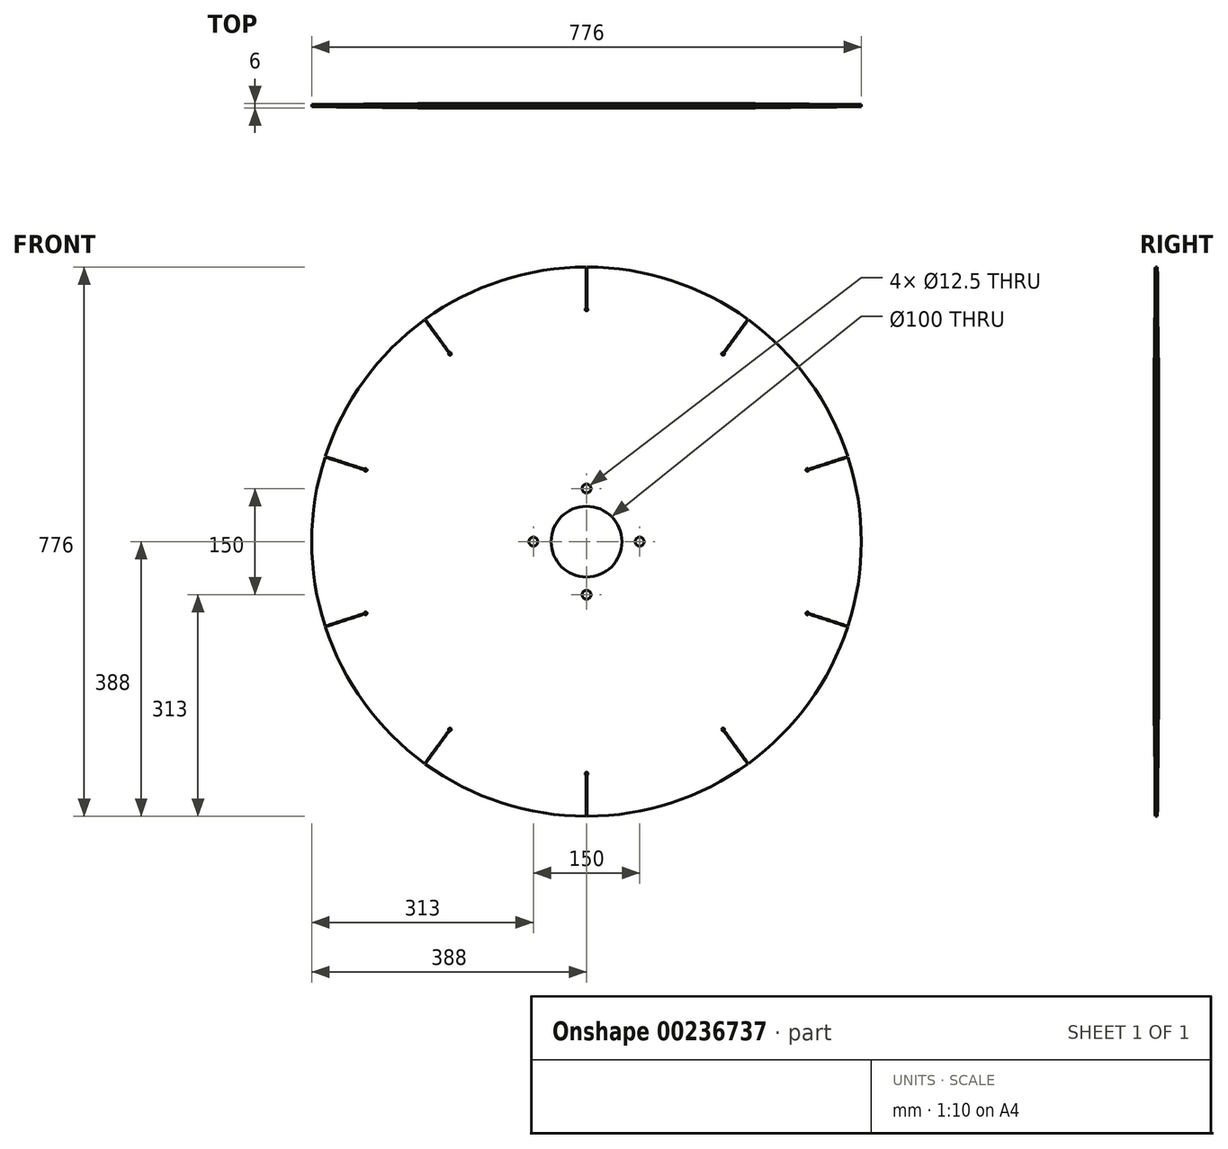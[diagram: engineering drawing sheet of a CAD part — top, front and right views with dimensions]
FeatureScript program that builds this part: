
annotation { "Feature Type Name" : "Feature", "Feature Type Description" : "" }
export const myFeature = defineFeature(function(context is Context, id is Id, definition is map)
    precondition{}
    {
        {
            var Q0;
            Q0=qCreatedBy(makeId("Front.planeOp"),FACE);
            var sketch = newSketch(context, id + "F0", { "sketchPlane" : qUnion([Q0])});
            skCircle(sketch, "E0", {"center": v(0, 0) * mm, "radius": 388 * mm});
            skSolve(sketch);
        }
        {
            var Q0;
            Q0 = qSketchRegion(id + "F0", true);
            extrude(context, id + "F1", {"entities" : qUnion([Q0]), "oppositeDirection" : true, "depth" : 6 * mm, "offsetDistance" : 25 * mm});
        }
        {
            var Q0;
            Q0=makeQuery(id+"F1.opExtrude","CAP_FACE",FACE,{"disambiguationData":[OSD([sQuery(id+"F0.wireOp",EDGE,"E0")])],"isStart":false});
            var sketch = newSketch(context, id + "F2", { "sketchPlane" : qUnion([Q0])});
            skCircle(sketch, "E1", {"center": v(0, 0) * mm, "radius": 50 * mm});
            skSolve(sketch);
        }
        {
            var Q0;
            Q0 = qSketchRegion(id + "F2", true);
            extrude(context, id + "F3", {"entities" : qUnion([Q0]), "operationType" : NewBodyOperationType.REMOVE, "endBound" : BoundingType.THROUGH_ALL, "oppositeDirection" : true, "depth" : 25 * mm, "offsetDistance" : 25 * mm});
        }
        {
            var Q0;
            Q0=makeQuery(id+"F1.opExtrude","CAP_EDGE",EDGE,{"disambiguationData":[OSD([sQuery(id+"F0.wireOp",EDGE,"E0")])],"isStart":true});
            var Q1;
            Q1=makeQuery(id+"F1.opExtrude","CAP_EDGE",EDGE,{"disambiguationData":[OSD([sQuery(id+"F0.wireOp",EDGE,"E0")])],"isStart":false});
            chamfer(context, id + "F4", {"entities" : qUnion([Q0, Q1]), "chamferType" : ChamferType.OFFSET_ANGLE, "width" : 150 * mm, "oppositeDirection" : false, "angle" : 0.56 * degree, "tangentPropagation" : true});
        }
        {
            var Q0;
            Q0=makeQuery(id+"F1.opExtrude","CAP_FACE",FACE,{"disambiguationData":[OSD([sQuery(id+"F0.wireOp",EDGE,"E0")])],"isStart":true});
            var sketch = newSketch(context, id + "F5", { "sketchPlane" : qUnion([Q0])});
            skCircle(sketch, "E2", {"center": v(0, 0) * mm, "radius": 75 * mm, "construction": true});
            skPoint(sketch, "E3", {"position": v(0, 75) * mm});
            skPoint(sketch, "E4", {"position": v(75, 0) * mm});
            skPoint(sketch, "E5", {"position": v(0, -75) * mm});
            skPoint(sketch, "E6", {"position": v(-75, 0) * mm});
            skSolve(sketch);
        }
        {
            var Q0;
            Q0=sQuery(id+"F5.wireOp",VERTEX,"E3");
            var Q1;
            Q1=sQuery(id+"F5.wireOp",VERTEX,"E4");
            var Q2;
            Q2=sQuery(id+"F5.wireOp",VERTEX,"E5");
            var Q3;
            Q3=sQuery(id+"F5.wireOp",VERTEX,"E6");
            var Q4;
            Q4=makeQuery(id+"F1.opExtrude","SWEPT_BODY",BODY,{"disambiguationData":[OSD([sQuery(id+"F0.wireOp",EDGE,"E0")])]});
            hole(context, id + "F6", {"style" : HoleStyle.SIMPLE, "endStyle" : HoleEndStyle.THROUGH, "holeDiameter" : 12.5 * mm, "majorDiameter" : 5 * mm, "isTappedThrough" : true, "tappedDepth" : 31.25 * mm, "tapClearance" : 3, "startFromSketch" : true, "locations" : qUnion([Q0, Q1, Q2, Q3]), "scope" : qUnion([Q4])});
        }
        {
            var Q0;
            Q0=makeQuery(id+"F1.opExtrude","CAP_FACE",FACE,{"disambiguationData":[OSD([sQuery(id+"F0.wireOp",EDGE,"E0")])],"isStart":true});
            var sketch = newSketch(context, id + "F7", { "sketchPlane" : qUnion([Q0])});
            skLineSegment(sketch, "E7.top", {"start": v(0, 417.47) * mm, "end": v(0.5, 417.47) * mm});
            skLineSegment(sketch, "E7.right", {"start": v(0.5, 329.94) * mm, "end": v(0.5, 417.47) * mm});
            skLineSegment(sketch, "E8.bottom", {"start": v(0, 417.47) * mm, "end": v(-0.5, 417.47) * mm});
            skLineSegment(sketch, "E8.left", {"start": v(0, 417.47) * mm, "end": v(0, 328) * mm, "construction": true});
            skLineSegment(sketch, "E8.right", {"start": v(-0.5, 417.47) * mm, "end": v(-0.5, 329.94) * mm});
            skArc(sketch, "E9", {"start": v(-0.5, 329.94) * mm, "mid": v(0, 326) * mm, "end": v(0.5, 329.94) * mm});
            skPoint(sketch, "E8.top.end.orphan", {"position": v(-0.5, 328) * mm});
            skPoint(sketch, "E10.1.0", {"position": v(-193.2, 265.06) * mm});
            skLineSegment(sketch, "E10.1.1", {"start": v(-245.38, 337.74) * mm, "end": v(-192.8, 265.36) * mm, "construction": true});
            skLineSegment(sketch, "E10.1.2", {"start": v(-193.53, 267.22) * mm, "end": v(-244.98, 338.04) * mm});
            skLineSegment(sketch, "E10.1.3", {"start": v(-245.79, 337.45) * mm, "end": v(-194.34, 266.63) * mm});
            skArc(sketch, "E10.1.4", {"start": v(-194.34, 266.63) * mm, "mid": v(-191.62, 263.74) * mm, "end": v(-193.53, 267.22) * mm});
            skLineSegment(sketch, "E10.1.5", {"start": v(-245.38, 337.74) * mm, "end": v(-245.79, 337.45) * mm});
            skLineSegment(sketch, "E10.1.6", {"start": v(-245.38, 337.74) * mm, "end": v(-244.98, 338.04) * mm});
            skPoint(sketch, "E10.2.0", {"position": v(-312.1, 100.88) * mm});
            skLineSegment(sketch, "E10.2.1", {"start": v(-397.04, 129) * mm, "end": v(-311.95, 101.36) * mm, "construction": true});
            skLineSegment(sketch, "E10.2.2", {"start": v(-313.63, 102.43) * mm, "end": v(-396.88, 129.48) * mm});
            skLineSegment(sketch, "E10.2.3", {"start": v(-397.2, 128.53) * mm, "end": v(-313.94, 101.48) * mm});
            skArc(sketch, "E10.2.4", {"start": v(-313.94, 101.48) * mm, "mid": v(-310.04, 100.74) * mm, "end": v(-313.63, 102.43) * mm});
            skLineSegment(sketch, "E10.2.5", {"start": v(-397.04, 129) * mm, "end": v(-397.2, 128.53) * mm});
            skLineSegment(sketch, "E10.2.6", {"start": v(-397.04, 129) * mm, "end": v(-396.88, 129.48) * mm});
            skPoint(sketch, "E10.3.0", {"position": v(-311.8, -101.83) * mm});
            skLineSegment(sketch, "E10.3.1", {"start": v(-397.04, -129) * mm, "end": v(-311.95, -101.36) * mm, "construction": true});
            skLineSegment(sketch, "E10.3.2", {"start": v(-313.94, -101.48) * mm, "end": v(-397.2, -128.53) * mm});
            skLineSegment(sketch, "E10.3.3", {"start": v(-396.88, -129.48) * mm, "end": v(-313.63, -102.43) * mm});
            skArc(sketch, "E10.3.4", {"start": v(-313.63, -102.43) * mm, "mid": v(-310.04, -100.74) * mm, "end": v(-313.94, -101.48) * mm});
            skLineSegment(sketch, "E10.3.5", {"start": v(-397.04, -129) * mm, "end": v(-396.88, -129.48) * mm});
            skLineSegment(sketch, "E10.3.6", {"start": v(-397.04, -129) * mm, "end": v(-397.2, -128.53) * mm});
            skPoint(sketch, "E10.4.0", {"position": v(-192.39, -265.65) * mm});
            skLineSegment(sketch, "E10.4.1", {"start": v(-245.38, -337.74) * mm, "end": v(-192.8, -265.36) * mm, "construction": true});
            skLineSegment(sketch, "E10.4.2", {"start": v(-194.34, -266.63) * mm, "end": v(-245.79, -337.45) * mm});
            skLineSegment(sketch, "E10.4.3", {"start": v(-244.98, -338.04) * mm, "end": v(-193.53, -267.22) * mm});
            skArc(sketch, "E10.4.4", {"start": v(-193.53, -267.22) * mm, "mid": v(-191.62, -263.74) * mm, "end": v(-194.34, -266.63) * mm});
            skLineSegment(sketch, "E10.4.5", {"start": v(-245.38, -337.74) * mm, "end": v(-244.98, -338.04) * mm});
            skLineSegment(sketch, "E10.4.6", {"start": v(-245.38, -337.74) * mm, "end": v(-245.79, -337.45) * mm});
            skPoint(sketch, "E10.5.0", {"position": v(0.5, -328) * mm});
            skLineSegment(sketch, "E10.5.1", {"start": v(0, -417.47) * mm, "end": v(0, -328) * mm, "construction": true});
            skLineSegment(sketch, "E10.5.2", {"start": v(-0.5, -329.94) * mm, "end": v(-0.5, -417.47) * mm});
            skLineSegment(sketch, "E10.5.3", {"start": v(0.5, -417.47) * mm, "end": v(0.5, -329.94) * mm});
            skArc(sketch, "E10.5.4", {"start": v(0.5, -329.94) * mm, "mid": v(0, -326) * mm, "end": v(-0.5, -329.94) * mm});
            skLineSegment(sketch, "E10.5.5", {"start": v(0, -417.47) * mm, "end": v(0.5, -417.47) * mm});
            skLineSegment(sketch, "E10.5.6", {"start": v(0, -417.47) * mm, "end": v(-0.5, -417.47) * mm});
            skPoint(sketch, "E10.6.0", {"position": v(193.2, -265.06) * mm});
            skLineSegment(sketch, "E10.6.1", {"start": v(245.38, -337.74) * mm, "end": v(192.8, -265.36) * mm, "construction": true});
            skLineSegment(sketch, "E10.6.2", {"start": v(193.53, -267.22) * mm, "end": v(244.98, -338.04) * mm});
            skLineSegment(sketch, "E10.6.3", {"start": v(245.79, -337.45) * mm, "end": v(194.34, -266.63) * mm});
            skArc(sketch, "E10.6.4", {"start": v(194.34, -266.63) * mm, "mid": v(191.62, -263.74) * mm, "end": v(193.53, -267.22) * mm});
            skLineSegment(sketch, "E10.6.5", {"start": v(245.38, -337.74) * mm, "end": v(245.79, -337.45) * mm});
            skLineSegment(sketch, "E10.6.6", {"start": v(245.38, -337.74) * mm, "end": v(244.98, -338.04) * mm});
            skPoint(sketch, "E10.7.0", {"position": v(312.1, -100.88) * mm});
            skLineSegment(sketch, "E10.7.1", {"start": v(397.04, -129) * mm, "end": v(311.95, -101.36) * mm, "construction": true});
            skLineSegment(sketch, "E10.7.2", {"start": v(313.63, -102.43) * mm, "end": v(396.88, -129.48) * mm});
            skLineSegment(sketch, "E10.7.3", {"start": v(397.2, -128.53) * mm, "end": v(313.94, -101.48) * mm});
            skArc(sketch, "E10.7.4", {"start": v(313.94, -101.48) * mm, "mid": v(310.04, -100.74) * mm, "end": v(313.63, -102.43) * mm});
            skLineSegment(sketch, "E10.7.5", {"start": v(397.04, -129) * mm, "end": v(397.2, -128.53) * mm});
            skLineSegment(sketch, "E10.7.6", {"start": v(397.04, -129) * mm, "end": v(396.88, -129.48) * mm});
            skPoint(sketch, "E10.center", {"position": v(0, 0) * mm});
            skPoint(sketch, "E11.0.8.0", {"position": v(311.8, 101.83) * mm});
            skLineSegment(sketch, "E11.1.8.0", {"start": v(397.04, 129) * mm, "end": v(311.95, 101.36) * mm, "construction": true});
            skLineSegment(sketch, "E11.4.8.0", {"start": v(313.94, 101.48) * mm, "end": v(397.2, 128.53) * mm});
            skLineSegment(sketch, "E11.7.8.0", {"start": v(396.88, 129.48) * mm, "end": v(313.63, 102.43) * mm});
            skArc(sketch, "E11.10.8.0", {"start": v(313.63, 102.43) * mm, "mid": v(310.04, 100.74) * mm, "end": v(313.94, 101.48) * mm});
            skLineSegment(sketch, "E11.14.8.0", {"start": v(397.04, 129) * mm, "end": v(396.88, 129.48) * mm});
            skLineSegment(sketch, "E11.17.8.0", {"start": v(397.04, 129) * mm, "end": v(397.2, 128.53) * mm});
            skPoint(sketch, "E11.0.9.0", {"position": v(192.39, 265.65) * mm});
            skLineSegment(sketch, "E11.1.9.0", {"start": v(245.38, 337.74) * mm, "end": v(192.8, 265.36) * mm, "construction": true});
            skLineSegment(sketch, "E11.4.9.0", {"start": v(194.34, 266.63) * mm, "end": v(245.79, 337.45) * mm});
            skLineSegment(sketch, "E11.7.9.0", {"start": v(244.98, 338.04) * mm, "end": v(193.53, 267.22) * mm});
            skArc(sketch, "E11.10.9.0", {"start": v(193.53, 267.22) * mm, "mid": v(191.62, 263.74) * mm, "end": v(194.34, 266.63) * mm});
            skLineSegment(sketch, "E11.14.9.0", {"start": v(245.38, 337.74) * mm, "end": v(244.98, 338.04) * mm});
            skLineSegment(sketch, "E11.17.9.0", {"start": v(245.38, 337.74) * mm, "end": v(245.79, 337.45) * mm});
            skSolve(sketch);
        }
        {
            var Q0;
            Q0 = qSketchRegion(id + "F7", true);
            extrude(context, id + "F8", {"entities" : qUnion([Q0]), "operationType" : NewBodyOperationType.REMOVE, "endBound" : BoundingType.THROUGH_ALL, "oppositeDirection" : true, "depth" : 25 * mm, "offsetDistance" : 25 * mm});
        }
    });
